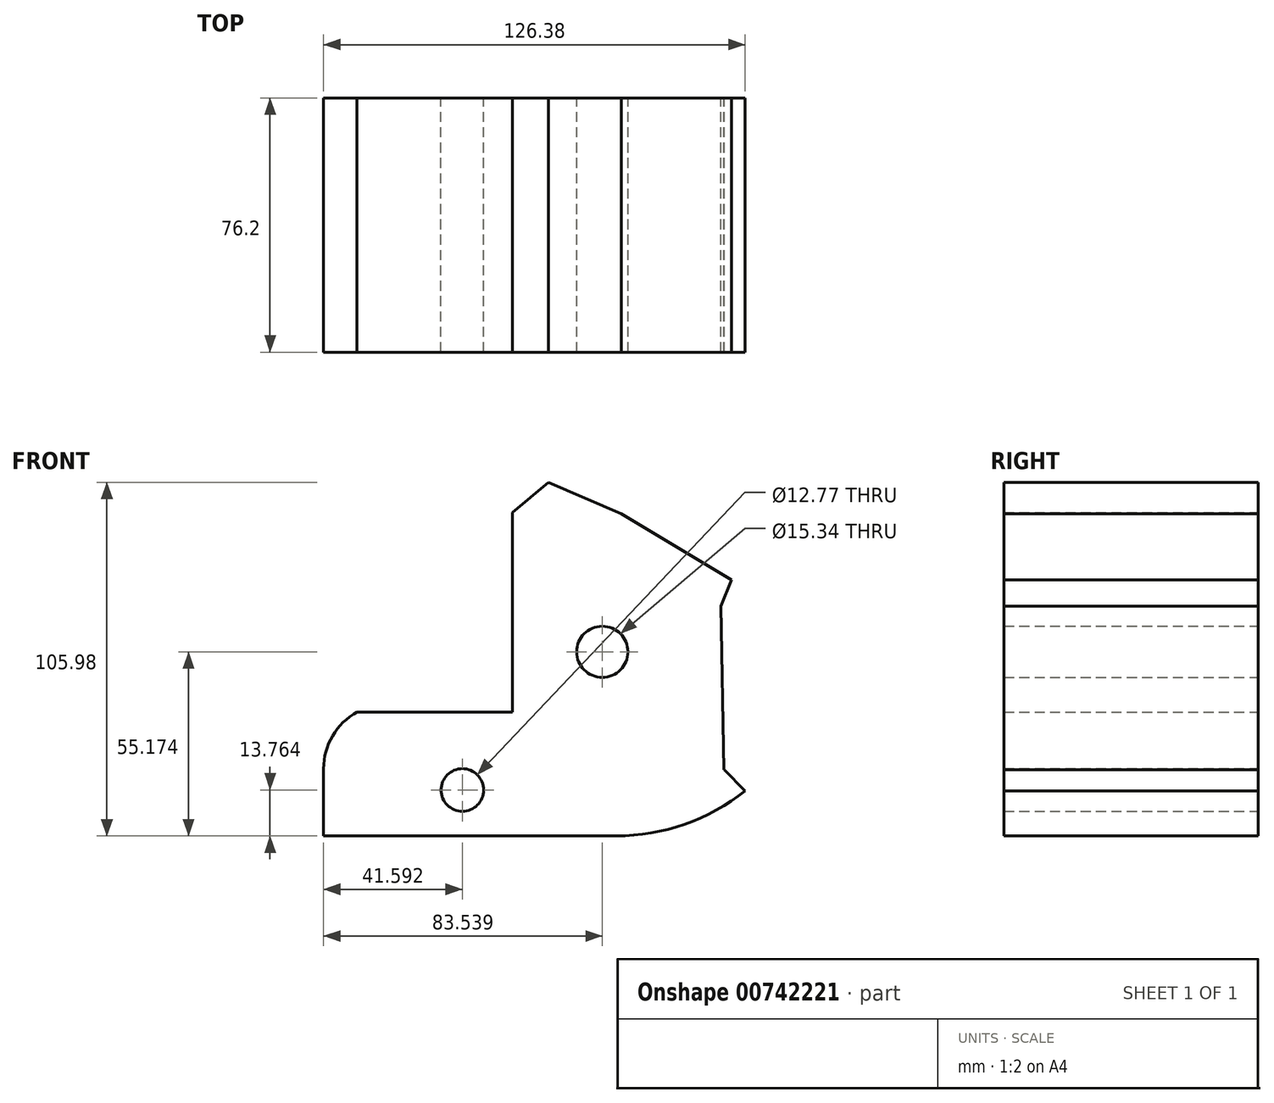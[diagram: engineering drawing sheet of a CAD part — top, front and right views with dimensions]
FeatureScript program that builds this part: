
annotation { "Feature Type Name" : "Feature", "Feature Type Description" : "" }
export const myFeature = defineFeature(function(context is Context, id is Id, definition is map)
    precondition{}
    {
        {
            var Q0;
            Q0=qCreatedBy(makeId("Front.planeOp"),FACE);
            var sketch = newSketch(context, id + "F0", { "sketchPlane" : qUnion([Q0])});
            skLineSegment(sketch, "E0", {"start": v(-59.58, -46.21) * mm, "end": v(-59.58, -25.46) * mm});
            skArc(sketch, "E1", {"start": v(-51.72, -14.78) * mm, "mid": v(-57.4, -18.83) * mm, "end": v(-59.58, -25.46) * mm});
            skLineSegment(sketch, "E2", {"start": v(-51.72, -14.78) * mm, "end": v(9.59, -14.78) * mm});
            skLineSegment(sketch, "E3", {"start": v(9.59, -14.78) * mm, "end": v(34.74, -38.67) * mm});
            skLineSegment(sketch, "E4", {"start": v(-59.58, -46.21) * mm, "end": v(0, -46.21) * mm});
            skLineSegment(sketch, "E5", {"start": v(0, -46.21) * mm, "end": v(0, -14.78) * mm});
            skLineSegment(sketch, "E6", {"start": v(0, -14.78) * mm, "end": v(9.59, -14.78) * mm});
            skArc(sketch, "E7", {"start": v(34.74, -38.67) * mm, "mid": v(48.48, -42.3) * mm, "end": v(58.95, -32.7) * mm});
            skLineSegment(sketch, "E8", {"start": v(58.95, -32.7) * mm, "end": v(52.66, -26.4) * mm});
            skLineSegment(sketch, "E9", {"start": v(52.66, -26.4) * mm, "end": v(30.42, -34.56) * mm});
            skLineSegment(sketch, "E10", {"start": v(21.83, -26.4) * mm, "end": v(44.93, -17.94) * mm});
            skLineSegment(sketch, "E11", {"start": v(44.93, -17.94) * mm, "end": v(44.93, 22.64) * mm});
            skLineSegment(sketch, "E12", {"start": v(44.93, 22.64) * mm, "end": v(51.72, 22.64) * mm});
            skLineSegment(sketch, "E13", {"start": v(51.72, 22.64) * mm, "end": v(52.66, -29.55) * mm});
            skLineSegment(sketch, "E14", {"start": v(44.93, 22.64) * mm, "end": v(12.73, 42.78) * mm});
            skLineSegment(sketch, "E15", {"start": v(12.73, 42.78) * mm, "end": v(21.85, 50.32) * mm});
            skLineSegment(sketch, "E16", {"start": v(21.85, 50.32) * mm, "end": v(54.87, 30.49) * mm});
            skLineSegment(sketch, "E17", {"start": v(54.87, 30.49) * mm, "end": v(51.72, 22.64) * mm});
            skLineSegment(sketch, "E18", {"start": v(12.73, 42.78) * mm, "end": v(-10.85, 50.65) * mm});
            skLineSegment(sketch, "E19", {"start": v(-10.85, 50.65) * mm, "end": v(0, 59.77) * mm});
            skLineSegment(sketch, "E20", {"start": v(0, 59.77) * mm, "end": v(21.85, 50.32) * mm});
            skLineSegment(sketch, "E21", {"start": v(-10.85, 50.65) * mm, "end": v(-10.85, -14.78) * mm});
            skLineSegment(sketch, "E22", {"start": v(0, -46.21) * mm, "end": v(20.28, -46.21) * mm});
            skArc(sketch, "E23", {"start": v(20.28, -46.21) * mm, "mid": v(40.76, -42.74) * mm, "end": v(58.95, -32.7) * mm});
            skLineSegment(sketch, "E24", {"start": v(-59.58, -46.21) * mm, "end": v(-67.43, -46.21) * mm});
            skLineSegment(sketch, "E25", {"start": v(-67.43, -46.21) * mm, "end": v(-67.43, -26.1) * mm});
            skArc(sketch, "E26", {"start": v(-67.43, -26.1) * mm, "mid": v(-64.73, -16.24) * mm, "end": v(-57.37, -9.12) * mm});
            skLineSegment(sketch, "E27", {"start": v(-57.37, -9.12) * mm, "end": v(-10.85, -9.12) * mm});
            skCircle(sketch, "E28", {"center": v(-25.84, -32.45) * mm, "radius": 6.39 * mm});
            skPoint(sketch, "E28.first.point", {"position": v(-32.22, -32.45) * mm});
            skPoint(sketch, "E28.second.point", {"position": v(-26.88, -38.75) * mm});
            skPoint(sketch, "E28.third.point", {"position": v(-19.65, -30.87) * mm});
            skCircle(sketch, "E29", {"center": v(16.1, 8.96) * mm, "radius": 7.67 * mm});
            skPoint(sketch, "E29.first.point", {"position": v(12.73, 15.85) * mm});
            skPoint(sketch, "E29.second.point", {"position": v(20.28, 2.53) * mm});
            skPoint(sketch, "E29.third.point", {"position": v(23.74, 9.77) * mm});
            skSolve(sketch);
        }
        {
            var Q0;
            Q0=makeQuery(id+"F0.imprint","IMPRINT",FACE,{"disambiguationData":[TD([[makeQuery(id+"F0.imprint","IMPRINT",EDGE,{"derivedFrom":sQuery(id+"F0.wireOp",EDGE,"E0")}),-1.0]])]});
            var Q1;
            Q1=makeQuery(id+"F0.imprint","IMPRINT",FACE,{"disambiguationData":[TD([[makeQuery(id+"F0.imprint","IMPRINT",EDGE,{"derivedFrom":sQuery(id+"F0.wireOp",EDGE,"E0")}),1.0]])]});
            var Q2;
            {var subQ0=sQuery(id+"F0.wireOp",EDGE,"E10");Q2=makeQuery(id+"F0.imprint","IMPRINT",FACE,{"disambiguationData":[TD([[makeQuery(id+"F0.imprint","IMPRINT",EDGE,{"derivedFrom":subQ0}),1.0]])]});}
            var Q3;
            {var subQ10=sQuery(id+"F0.wireOp",EDGE,"E5");Q3=makeQuery(id+"F0.imprint","IMPRINT",FACE,{"disambiguationData":[TD([[makeQuery(id+"F0.imprint","IMPRINT",EDGE,{"derivedFrom":subQ10}),-1.0]])]});}
            var Q4;
            {var subQ8=sQuery(id+"F0.wireOp",EDGE,"E8");Q4=makeQuery(id+"F0.imprint","IMPRINT",FACE,{"disambiguationData":[TD([[makeQuery(id+"F0.imprint","IMPRINT",EDGE,{"derivedFrom":subQ8}),1.0]])]});}
            var Q5;
            {var subQ0=sQuery(id+"F0.wireOp",EDGE,"E10");Q5=makeQuery(id+"F0.imprint","IMPRINT",FACE,{"disambiguationData":[TD([[makeQuery(id+"F0.imprint","IMPRINT",EDGE,{"derivedFrom":subQ0}),-1.0]])]});}
            var Q6;
            Q6=makeQuery(id+"F0.imprint","IMPRINT",FACE,{"disambiguationData":[TD([[makeQuery(id+"F0.imprint","IMPRINT",EDGE,{"derivedFrom":sQuery(id+"F0.wireOp",EDGE,"E12")}),1.0]])]});
            var Q7;
            Q7=makeQuery(id+"F0.imprint","IMPRINT",FACE,{"disambiguationData":[TD([[makeQuery(id+"F0.imprint","IMPRINT",EDGE,{"derivedFrom":sQuery(id+"F0.wireOp",EDGE,"E15")}),1.0]])]});
            extrude(context, id + "F1", {"entities" : qUnion([Q0, Q1, Q2, Q3, Q4, Q5, Q6, Q7]), "depth" : 76.2 * mm, "offsetDistance" : 25.4 * mm});
        }
    });
